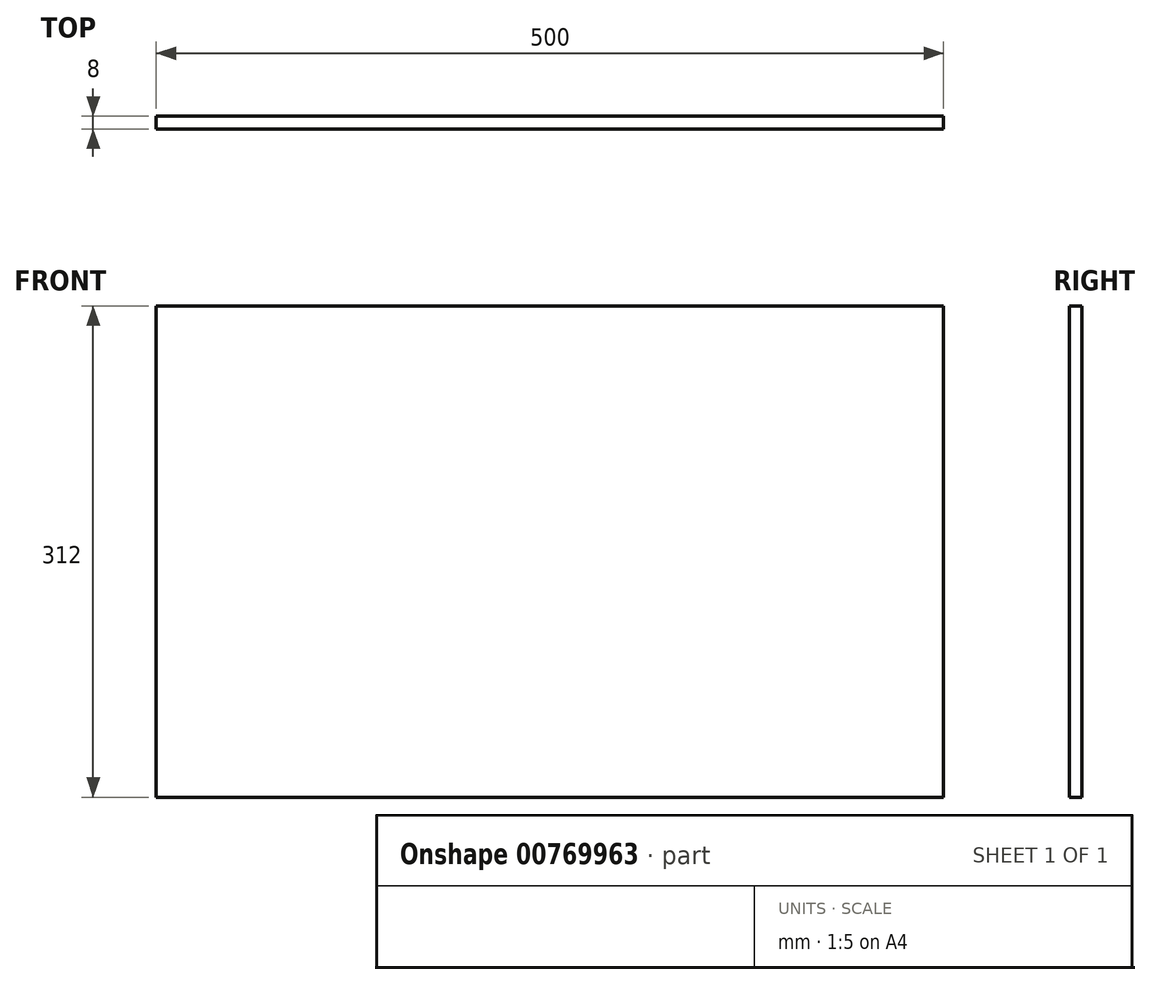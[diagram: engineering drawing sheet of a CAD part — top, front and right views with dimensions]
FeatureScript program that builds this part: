
annotation { "Feature Type Name" : "Feature", "Feature Type Description" : "" }
export const myFeature = defineFeature(function(context is Context, id is Id, definition is map)
    precondition{}
    {
        {
            var Q0;
            Q0=qCreatedBy(makeId("Front.planeOp"),FACE);
            var sketch = newSketch(context, id + "F0", { "sketchPlane" : qUnion([Q0])});
            skLineSegment(sketch, "E0.bottom", {"start": v(-230.63, 152.32) * mm, "end": v(269.37, 152.32) * mm});
            skLineSegment(sketch, "E0.top", {"start": v(-230.63, -159.68) * mm, "end": v(269.37, -159.68) * mm});
            skLineSegment(sketch, "E0.left", {"start": v(-230.63, 152.32) * mm, "end": v(-230.63, -159.68) * mm});
            skLineSegment(sketch, "E0.right", {"start": v(269.37, 152.32) * mm, "end": v(269.37, -159.68) * mm});
            skSolve(sketch);
        }
        {
            var Q0;
            Q0 = qSketchRegion(id + "F0", true);
            extrude(context, id + "F1", {"entities" : qUnion([Q0]), "depth" : 8 * mm, "offsetDistance" : 25 * mm});
        }
    });
